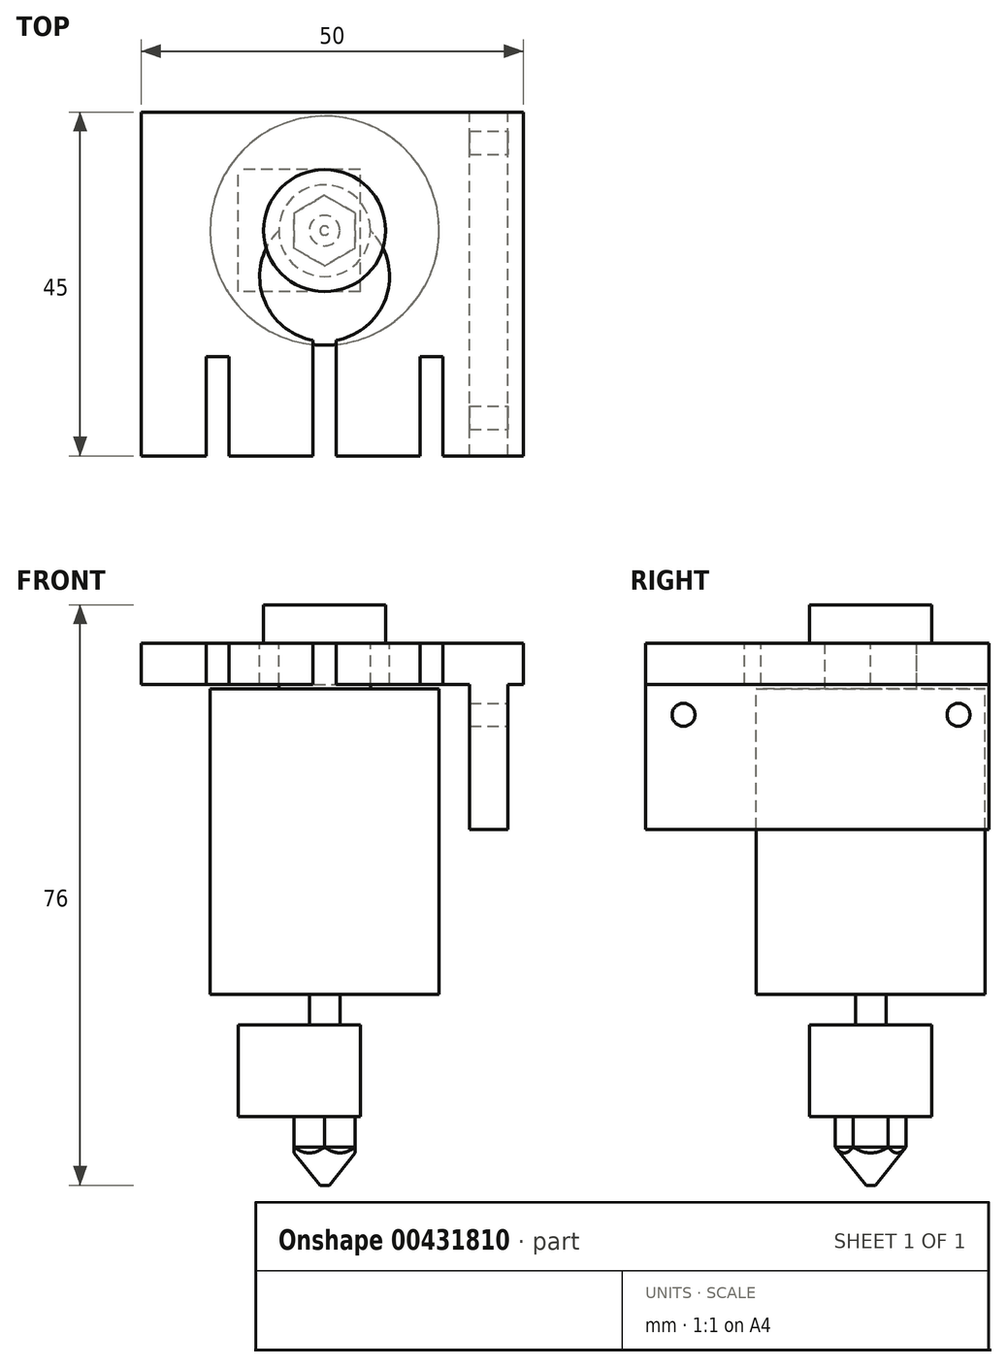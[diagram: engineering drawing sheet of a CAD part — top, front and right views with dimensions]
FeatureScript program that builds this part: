
annotation { "Feature Type Name" : "Feature", "Feature Type Description" : "" }
export const myFeature = defineFeature(function(context is Context, id is Id, definition is map)
    precondition{}
    {
        {
            var Q0;
            Q0=qCreatedBy(makeId("Top.planeOp"),FACE);
            var sketch = newSketch(context, id + "F0", { "sketchPlane" : qUnion([Q0])});
            skCircle(sketch, "E0", {"center": v(0, 0) * mm, "radius": 8 * mm});
            skSolve(sketch);
        }
        {
            var Q0;
            Q0 = qSketchRegion(id + "F0", true);
            extrude(context, id + "F1", {"entities" : qUnion([Q0]), "oppositeDirection" : true, "depth" : 5 * mm});
        }
        {
            var Q0;
            Q0=makeQuery(id+"F1.opExtrude","CAP_FACE",FACE,{"disambiguationData":[OSD([sQuery(id+"F0.wireOp",EDGE,"E0")])],"isStart":false});
            var sketch = newSketch(context, id + "F2", { "sketchPlane" : qUnion([Q0])});
            skCircle(sketch, "E1", {"center": v(0, 0) * mm, "radius": 6 * mm});
            skCircle(sketch, "E2", {"center": v(0, 0) * mm, "radius": 2 * mm});
            skSolve(sketch);
        }
        {
            var Q0;
            Q0 = qSketchRegion(id + "F2", true);
            extrude(context, id + "F3", {"entities" : qUnion([Q0]), "operationType" : NewBodyOperationType.ADD, "depth" : 6 * mm});
        }
        {
            var Q0;
            Q0=makeQuery(id+"F3.opExtrude","CAP_FACE",FACE,{"disambiguationData":[OSD([sQuery(id+"F2.wireOp",EDGE,"E1")])],"isStart":false});
            var sketch = newSketch(context, id + "F4", { "sketchPlane" : qUnion([Q0])});
            skCircle(sketch, "E3", {"center": v(0, 0) * mm, "radius": 15 * mm});
            skSolve(sketch);
        }
        {
            var Q0;
            Q0 = qSketchRegion(id + "F4", true);
            extrude(context, id + "F5", {"entities" : qUnion([Q0]), "operationType" : NewBodyOperationType.ADD, "depth" : 40 * mm});
        }
        {
            var Q0;
            Q0=makeQuery(id+"F2.imprint","IMPRINT",FACE,{"disambiguationData":[TD([[makeQuery(id+"F2.imprint","IMPRINT",EDGE,{"derivedFrom":sQuery(id+"F2.wireOp",EDGE,"E2")}),1.0]])]});
            extrude(context, id + "F6", {"entities" : qUnion([Q0]), "operationType" : NewBodyOperationType.ADD, "depth" : 50 * mm});
        }
        {
            var Q0;
            Q0=makeQuery(id+"F6.opExtrude","CAP_FACE",FACE,{"disambiguationData":[OSD([sQuery(id+"F2.wireOp",EDGE,"E2")])],"isStart":false});
            var sketch = newSketch(context, id + "F7", { "sketchPlane" : qUnion([Q0])});
            skLineSegment(sketch, "E4.bottom", {"start": v(4.7, 8) * mm, "end": v(-11.3, 8) * mm});
            skLineSegment(sketch, "E4.top", {"start": v(4.7, -8) * mm, "end": v(-11.3, -8) * mm});
            skLineSegment(sketch, "E4.left", {"start": v(4.7, 8) * mm, "end": v(4.7, -8) * mm});
            skLineSegment(sketch, "E4.right", {"start": v(-11.3, 8) * mm, "end": v(-11.3, -8) * mm});
            skSolve(sketch);
        }
        {
            var Q0;
            Q0=makeQuery(id+"F7.imprint","IMPRINT",FACE,{"disambiguationData":[TD([[makeQuery(id+"F7.imprint","IMPRINT",EDGE,{"derivedFrom":makeQuery(id+"F6.opExtrude","CAP_EDGE",EDGE,{"disambiguationData":[OSD([sQuery(id+"F2.wireOp",EDGE,"E2")])],"isStart":false})}),1.0]])]});
            var Q1;
            Q1=makeQuery(id+"F7.imprint","IMPRINT",FACE,{"disambiguationData":[TD([[makeQuery(id+"F7.imprint","IMPRINT",EDGE,{"derivedFrom":sQuery(id+"F7.wireOp",EDGE,"E4.bottom")}),1.0]])]});
            extrude(context, id + "F8", {"entities" : qUnion([Q0, Q1]), "operationType" : NewBodyOperationType.ADD, "depth" : 12 * mm});
        }
        {
            var Q0;
            Q0=makeQuery(id+"F8.opExtrude","CAP_FACE",FACE,{"disambiguationData":[OSD([sQuery(id+"F7.wireOp",EDGE,"E4.bottom"),sQuery(id+"F7.wireOp",EDGE,"E4.top"),sQuery(id+"F7.wireOp",EDGE,"E4.left"),sQuery(id+"F7.wireOp",EDGE,"E4.right")])],"isStart":false});
            var sketch = newSketch(context, id + "F9", { "sketchPlane" : qUnion([Q0])});
            skCircle(sketch, "E5.cCircle", {"center": v(0, 0) * mm, "radius": 4 * mm, "construction": true});
            skLineSegment(sketch, "E5.0", {"start": v(0, -4.62) * mm, "end": v(-4, -2.3) * mm});
            skLineSegment(sketch, "E5.1", {"start": v(-4, -2.3) * mm, "end": v(-4, 2.3) * mm});
            skLineSegment(sketch, "E5.2", {"start": v(-4, 2.3) * mm, "end": v(0, 4.62) * mm});
            skLineSegment(sketch, "E5.3", {"start": v(0, 4.62) * mm, "end": v(4, 2.3) * mm});
            skLineSegment(sketch, "E5.4", {"start": v(4, 2.3) * mm, "end": v(4, -2.3) * mm});
            skLineSegment(sketch, "E5.5", {"start": v(4, -2.3) * mm, "end": v(0, -4.62) * mm});
            skPoint(sketch, "E5.0.midPoint", {"position": v(-2, -3.46) * mm});
            skSolve(sketch);
        }
        {
            var Q0;
            Q0=makeQuery(id+"F9.imprint","IMPRINT",FACE,{"disambiguationData":[TD([[makeQuery(id+"F9.imprint","IMPRINT",EDGE,{"derivedFrom":sQuery(id+"F9.wireOp",EDGE,"E5.0")}),-1.0]])]});
            extrude(context, id + "F10", {"entities" : qUnion([Q0]), "operationType" : NewBodyOperationType.ADD, "depth" : 4 * mm});
        }
        {
            var Q0;
            Q0=makeQuery(id+"F10.opExtrude","CAP_FACE",FACE,{"disambiguationData":[OSD([sQuery(id+"F9.wireOp",EDGE,"E5.0"),sQuery(id+"F9.wireOp",EDGE,"E5.1"),sQuery(id+"F9.wireOp",EDGE,"E5.2"),sQuery(id+"F9.wireOp",EDGE,"E5.3"),sQuery(id+"F9.wireOp",EDGE,"E5.4"),sQuery(id+"F9.wireOp",EDGE,"E5.5")])],"isStart":false});
            var sketch = newSketch(context, id + "F11", { "sketchPlane" : qUnion([Q0])});
            skCircle(sketch, "E6", {"center": v(0, 0) * mm, "radius": 4.62 * mm});
            skSolve(sketch);
        }
        {
            var Q0;
            Q0=makeQuery(id+"F11.imprint","IMPRINT",FACE,{"disambiguationData":[TD([[makeQuery(id+"F11.imprint","IMPRINT",EDGE,{"derivedFrom":makeQuery(id+"F10.opExtrude","CAP_EDGE",EDGE,{"disambiguationData":[OSD([sQuery(id+"F9.wireOp",EDGE,"E5.0")])],"isStart":false})}),-1.0]])]});
            cPlane(context, id + "F12", {"entities" : qUnion([Q0]), "cplaneType" : CPlaneType.OFFSET, "offset" : 5 * mm, "width" : 150 * mm, "height" : 150 * mm});
        }
        {
            var Q0;
            Q0=qCreatedBy(id+"F12.planeOp",FACE);
            var sketch = newSketch(context, id + "F13", { "sketchPlane" : qUnion([Q0])});
            skCircle(sketch, "E7", {"center": v(0, 0) * mm, "radius": 0.6 * mm});
            skSolve(sketch);
        }
        {
            var Q0;
            Q0 = qSketchRegion(id + "F13", true);
            var Q1;
            Q1 = qSketchRegion(id + "F11", true);
            loft(context, id + "F14", {"sheetProfilesArray" : [{ "sheetProfileEntities" : qUnion([Q0]) }, { "sheetProfileEntities" : qUnion([Q1]) }]});
        }
        {
            var Q0;
            Q0 = qSketchRegion(id + "F9", true);
            extrude(context, id + "F15", {"entities" : qUnion([Q0]), "depth" : 9 * mm});
        }
        {
            var Q0;
            {var subQ1=makeQuery(id+"F10.opExtrude","CAP_EDGE",EDGE,{"disambiguationData":[OSD([sQuery(id+"F9.wireOp",EDGE,"E5.3")])],"isStart":false});Q0=makeQuery(id+"F14.opLoft","SWEPT_BODY",BODY,{"disambiguationData":[OSD([makeQuery(id+"F11.imprint","IMPRINT",FACE,{"disambiguationData":[TD([[makeQuery(id+"F11.imprint","IMPRINT",EDGE,{"derivedFrom":subQ1}),1.0]])]}),makeQuery(id+"F13.imprint","IMPRINT",FACE,{"disambiguationData":[TD([[makeQuery(id+"F13.imprint","IMPRINT",EDGE,{"derivedFrom":sQuery(id+"F13.wireOp",EDGE,"E7")}),1.0]])]})])]});}
            var Q1;
            Q1=makeQuery(id+"F15.opExtrude","SWEPT_BODY",BODY,{"disambiguationData":[OSD([sQuery(id+"F9.wireOp",EDGE,"E5.0"),sQuery(id+"F9.wireOp",EDGE,"E5.1"),sQuery(id+"F9.wireOp",EDGE,"E5.2"),sQuery(id+"F9.wireOp",EDGE,"E5.3"),sQuery(id+"F9.wireOp",EDGE,"E5.4"),sQuery(id+"F9.wireOp",EDGE,"E5.5")])]});
            booleanBodies(context, id + "F16", {"operationType" : BooleanOperationType.INTERSECTION, "tools" : qUnion([Q0, Q1])});
        }
        {
            var Q0;
            Q0=makeQuery(id+"F1.opExtrude","CAP_FACE",FACE,{"disambiguationData":[OSD([sQuery(id+"F0.wireOp",EDGE,"E0")])],"isStart":false});
            var sketch = newSketch(context, id + "F17", { "sketchPlane" : qUnion([Q0])});
            skArc(sketch, "E8", {"start": v(-6, -0.02) * mm, "mid": v(0, -6) * mm, "end": v(6, -0.02) * mm});
            skPoint(sketch, "E9", {"position": v(0, 6) * mm});
            skArc(sketch, "E10", {"start": v(6, -0.02) * mm, "mid": v(8.11, 8.54) * mm, "end": v(1.5, 14.37) * mm});
            skLineSegment(sketch, "E11.bottom", {"start": v(-24, 29.5) * mm, "end": v(-15.5, 29.5) * mm});
            skLineSegment(sketch, "E11.top", {"start": v(-24, -15.5) * mm, "end": v(24, -15.5) * mm});
            skLineSegment(sketch, "E11.left", {"start": v(-24, 29.5) * mm, "end": v(-24, -15.5) * mm});
            skLineSegment(sketch, "E11.right", {"start": v(24, 29.5) * mm, "end": v(24, -15.5) * mm});
            skLineSegment(sketch, "E12.left", {"start": v(1.5, 29.5) * mm, "end": v(1.5, 14.37) * mm});
            skLineSegment(sketch, "E12.right", {"start": v(-1.5, 29.5) * mm, "end": v(-1.5, 14.37) * mm});
            skLineSegment(sketch, "E13.trimOffspring", {"start": v(1.5, 29.5) * mm, "end": v(12.5, 29.5) * mm});
            skArc(sketch, "E14.trimOffspring", {"start": v(-1.5, 14.37) * mm, "mid": v(-8.11, 8.54) * mm, "end": v(-6, -0.02) * mm});
            skLineSegment(sketch, "E15.top", {"start": v(12.5, 16.5) * mm, "end": v(15.5, 16.5) * mm});
            skLineSegment(sketch, "E15.left", {"start": v(12.5, 29.5) * mm, "end": v(12.5, 16.5) * mm});
            skLineSegment(sketch, "E15.right", {"start": v(15.5, 29.5) * mm, "end": v(15.5, 16.5) * mm});
            skLineSegment(sketch, "E16.top", {"start": v(-12.5, 16.5) * mm, "end": v(-15.5, 16.5) * mm});
            skLineSegment(sketch, "E16.left", {"start": v(-12.5, 29.5) * mm, "end": v(-12.5, 16.5) * mm});
            skLineSegment(sketch, "E16.right", {"start": v(-15.5, 29.5) * mm, "end": v(-15.5, 16.5) * mm});
            skLineSegment(sketch, "E17.trimOffspring", {"start": v(-12.5, 29.5) * mm, "end": v(-1.5, 29.5) * mm});
            skLineSegment(sketch, "E18.trimOffspring", {"start": v(15.5, 29.5) * mm, "end": v(24, 29.5) * mm});
            skSolve(sketch);
        }
        {
            var Q0;
            Q0 = qSketchRegion(id + "F17", true);
            extrude(context, id + "F18", {"entities" : qUnion([Q0]), "depth" : 5.4 * mm});
        }
        {
            var Q0;
            Q0=makeQuery(id+"F18.opExtrude","SWEPT_FACE",FACE,{"disambiguationData":[OSD([sQuery(id+"F17.wireOp",EDGE,"E11.right")])]});
            var sketch = newSketch(context, id + "F19", { "sketchPlane" : qUnion([Q0])});
            skLineSegment(sketch, "E19.bottom", {"start": v(-29.5, -5) * mm, "end": v(15.5, -5) * mm});
            skLineSegment(sketch, "E19.top", {"start": v(-29.5, -29.4) * mm, "end": v(15.5, -29.4) * mm});
            skLineSegment(sketch, "E19.left", {"start": v(-29.5, -5) * mm, "end": v(-29.5, -29.4) * mm});
            skLineSegment(sketch, "E19.right", {"start": v(15.5, -5) * mm, "end": v(15.5, -29.4) * mm});
            skLineSegment(sketch, "E20", {"start": v(-29.5, -14.4) * mm, "end": v(15.5, -14.4) * mm, "construction": true});
            skCircle(sketch, "E21", {"center": v(11.5, -14.4) * mm, "radius": 1.5 * mm});
            skCircle(sketch, "E22", {"center": v(-24.5, -14.4) * mm, "radius": 1.5 * mm});
            skSolve(sketch);
        }
        {
            var Q0;
            {var subQ0=sQuery(id+"F19.wireOp",EDGE,"E19.bottom");Q0=makeQuery(id+"F19.imprint","IMPRINT",FACE,{"disambiguationData":[TD([[makeQuery(id+"F19.imprint","IMPRINT",EDGE,{"derivedFrom":subQ0}),-1.0]])]});}
            extrude(context, id + "F20", {"entities" : qUnion([Q0]), "operationType" : NewBodyOperationType.ADD, "depth" : 2 * mm});
        }
        {
            var Q0;
            {var subQ2=sQuery(id+"F19.wireOp",EDGE,"E19.top");Q0=makeQuery(id+"F19.imprint","IMPRINT",FACE,{"disambiguationData":[TD([[makeQuery(id+"F19.imprint","IMPRINT",EDGE,{"derivedFrom":subQ2}),1.0]])]});}
            extrude(context, id + "F21", {"entities" : qUnion([Q0]), "operationType" : NewBodyOperationType.ADD, "oppositeDirection" : true, "depth" : 5 * mm});
        }
    });
